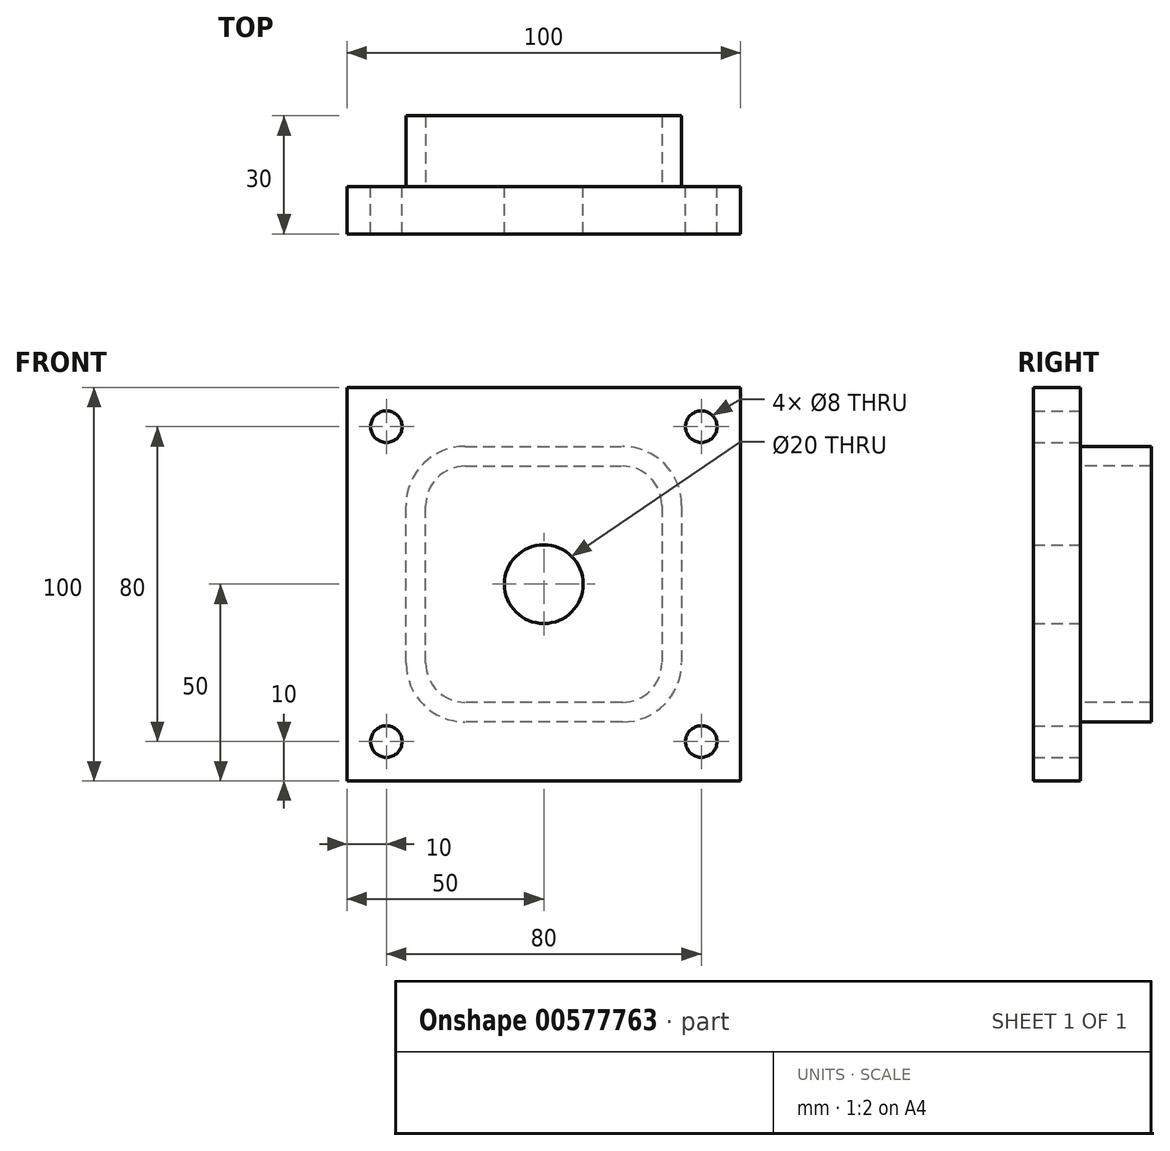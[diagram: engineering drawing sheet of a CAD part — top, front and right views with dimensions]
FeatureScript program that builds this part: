
annotation { "Feature Type Name" : "Feature", "Feature Type Description" : "" }
export const myFeature = defineFeature(function(context is Context, id is Id, definition is map)
    precondition{}
    {
        {
            var Q0;
            Q0=qCreatedBy(makeId("Front.planeOp"),FACE);
            var sketch = newSketch(context, id + "F0", { "sketchPlane" : qUnion([Q0])});
            skLineSegment(sketch, "E0.bottom", {"start": v(50, -50) * mm, "end": v(-50, -50) * mm});
            skLineSegment(sketch, "E0.top", {"start": v(50, 50) * mm, "end": v(-50, 50) * mm});
            skLineSegment(sketch, "E0.left", {"start": v(50, -50) * mm, "end": v(50, 50) * mm});
            skLineSegment(sketch, "E0.right", {"start": v(-50, -50) * mm, "end": v(-50, 50) * mm});
            skPoint(sketch, "E0.middle", {"position": v(0, 0) * mm});
            skCircle(sketch, "E1", {"center": v(40, -40) * mm, "radius": 4 * mm});
            skCircle(sketch, "E2", {"center": v(40, 40) * mm, "radius": 4 * mm});
            skCircle(sketch, "E3", {"center": v(-40, 40) * mm, "radius": 4 * mm});
            skCircle(sketch, "E4", {"center": v(-40, -40) * mm, "radius": 4 * mm});
            skCircle(sketch, "E5", {"center": v(0, 0) * mm, "radius": 10 * mm});
            skSolve(sketch);
        }
        {
            var Q0;
            Q0 = qSketchRegion(id + "F0", true);
            extrude(context, id + "F1", {"entities" : qUnion([Q0]), "depth" : 12 * mm, "offsetDistance" : 25 * mm});
        }
        {
            var Q0;
            Q0=makeQuery(id+"F1.opExtrude","CAP_FACE",FACE,{"disambiguationData":[OSD([sQuery(id+"F0.wireOp",EDGE,"E0.bottom"),sQuery(id+"F0.wireOp",EDGE,"E0.top"),sQuery(id+"F0.wireOp",EDGE,"E0.left"),sQuery(id+"F0.wireOp",EDGE,"E0.right"),sQuery(id+"F0.wireOp",EDGE,"E1"),sQuery(id+"F0.wireOp",EDGE,"E2"),sQuery(id+"F0.wireOp",EDGE,"E3"),sQuery(id+"F0.wireOp",EDGE,"E4"),sQuery(id+"F0.wireOp",EDGE,"E5")])],"isStart":true});
            var sketch = newSketch(context, id + "F2", { "sketchPlane" : qUnion([Q0])});
            skLineSegment(sketch, "E6", {"start": v(-35, 20) * mm, "end": v(-35, -20) * mm});
            skLineSegment(sketch, "E7", {"start": v(-20, -35) * mm, "end": v(20, -35) * mm});
            skLineSegment(sketch, "E8", {"start": v(35, -20) * mm, "end": v(35, 20) * mm});
            skLineSegment(sketch, "E9", {"start": v(20, 35) * mm, "end": v(-20, 35) * mm});
            skArc(sketch, "E10", {"start": v(-35, -20) * mm, "mid": v(-30.6, -30.6) * mm, "end": v(-20, -35) * mm});
            skArc(sketch, "E11", {"start": v(-20, 35) * mm, "mid": v(-30.6, 30.6) * mm, "end": v(-35, 20) * mm});
            skArc(sketch, "E12", {"start": v(20, -35) * mm, "mid": v(30.6, -30.6) * mm, "end": v(35, -20) * mm});
            skArc(sketch, "E13", {"start": v(35, 20) * mm, "mid": v(30.6, 30.6) * mm, "end": v(20, 35) * mm});
            skLineSegment(sketch, "E14", {"start": v(-30, 20) * mm, "end": v(-30, -20) * mm});
            skLineSegment(sketch, "E15", {"start": v(-20, -30) * mm, "end": v(20, -30) * mm});
            skLineSegment(sketch, "E16", {"start": v(30, -20) * mm, "end": v(30, 20) * mm});
            skLineSegment(sketch, "E17", {"start": v(20, 30) * mm, "end": v(-20, 30) * mm});
            skArc(sketch, "E18", {"start": v(-30, -20) * mm, "mid": v(-27.07, -27.07) * mm, "end": v(-20, -30) * mm});
            skArc(sketch, "E19", {"start": v(20, -30) * mm, "mid": v(27.07, -27.07) * mm, "end": v(30, -20) * mm});
            skArc(sketch, "E20", {"start": v(30, 20) * mm, "mid": v(27.07, 27.07) * mm, "end": v(20, 30) * mm});
            skArc(sketch, "E21", {"start": v(-20, 30) * mm, "mid": v(-27.07, 27.07) * mm, "end": v(-30, 20) * mm});
            skSolve(sketch);
        }
        {
            var Q0;
            Q0=makeQuery(id+"F2.imprint","IMPRINT",FACE,{"disambiguationData":[TD([[makeQuery(id+"F2.imprint","IMPRINT",EDGE,{"derivedFrom":sQuery(id+"F2.wireOp",EDGE,"E6")}),1.0]])]});
            extrude(context, id + "F3", {"entities" : qUnion([Q0]), "operationType" : NewBodyOperationType.ADD, "depth" : 18 * mm, "offsetDistance" : 25 * mm});
        }
    });
